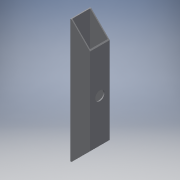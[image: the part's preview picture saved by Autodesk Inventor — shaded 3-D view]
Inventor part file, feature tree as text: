
AUTODESK INVENTOR PART (.ipt)
format: ipt  version: 2018 (Build 220112000, 112)  size: 115,200 bytes
history: native  units: mm
features: extrude x2, chamfer x2, sketch x2, other x1
ambient origin geometry x8: Origin, YZ Plane, XZ Plane, XY Plane, X Axis, Y Axis, Z Axis, Center Point
bodies: Body1 (feature_tree)
feature tree (7):
  other  "ソリッド1"
  extrude  "押し出し1"  Depth=32.0mm
  extrude  "押し出し2"  Depth=32.0mm
  chamfer  "面取り2"  Distance=1.6mm
  chamfer  "面取り3"  Distance=200.0mm
  sketch  "スケッチ1"
  sketch  "スケッチ3"
